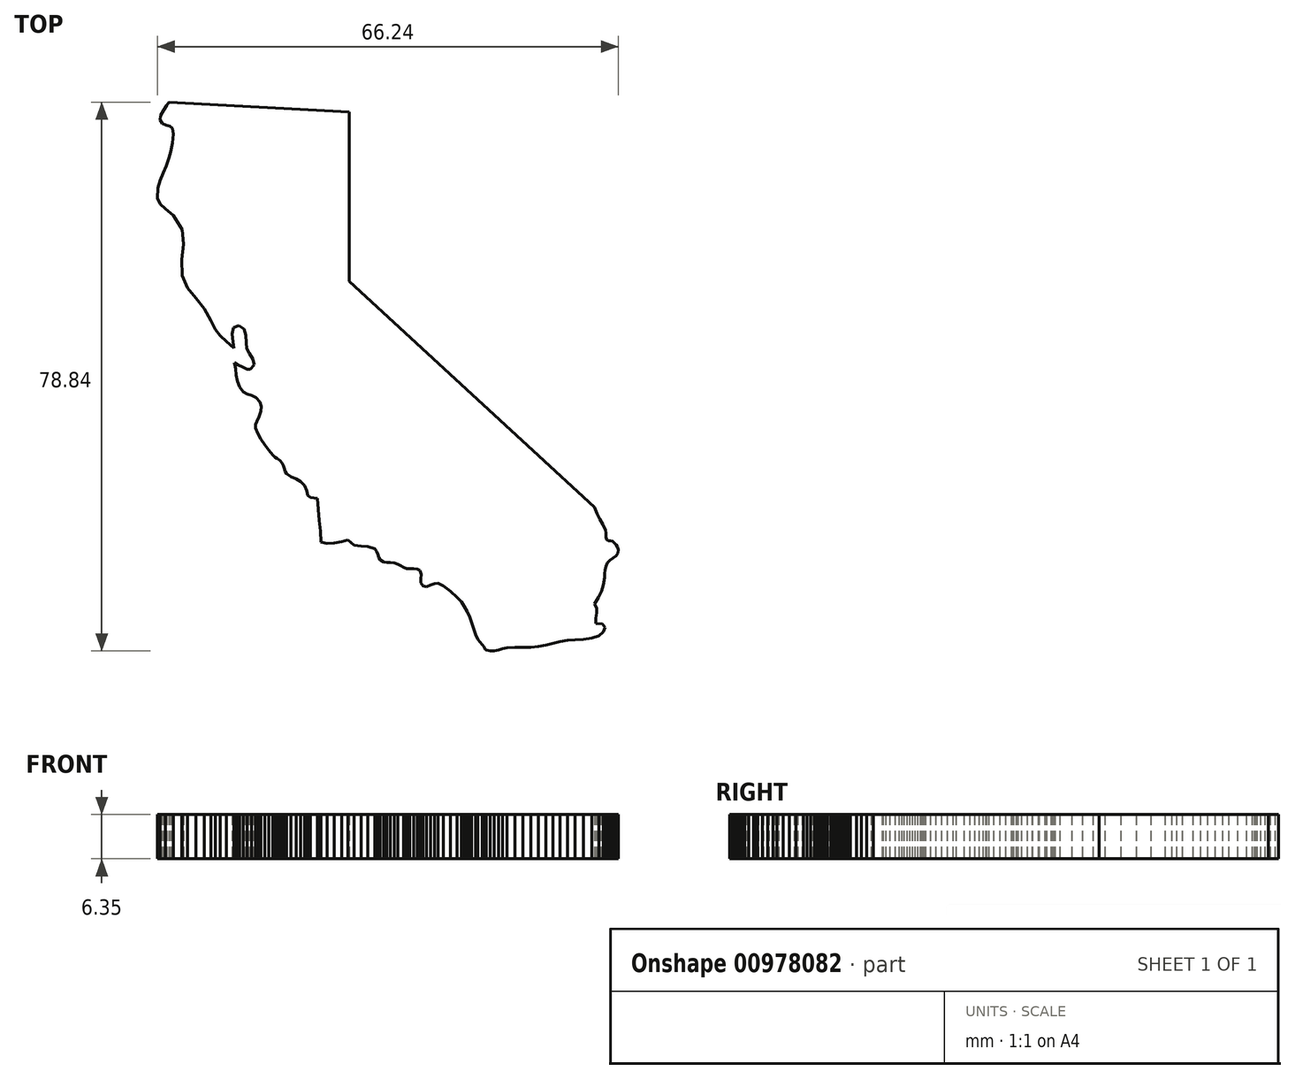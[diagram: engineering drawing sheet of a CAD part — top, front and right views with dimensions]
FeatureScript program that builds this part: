
annotation { "Feature Type Name" : "Feature", "Feature Type Description" : "" }
export const myFeature = defineFeature(function(context is Context, id is Id, definition is map)
    precondition{}
    {
        {
            var Q0;
            Q0=qCreatedBy(makeId("Top.planeOp"),FACE);
            var sketch = newSketch(context, id + "F0", { "sketchPlane" : qUnion([Q0])});
            skLineSegment(sketch, "E0", {"start": v(29.7, -18.77) * mm, "end": v(20.88, -10.66) * mm});
            skLineSegment(sketch, "E1", {"start": v(20.88, -10.66) * mm, "end": v(12.07, -2.55) * mm});
            skLineSegment(sketch, "E2", {"start": v(12.07, -2.55) * mm, "end": v(3.26, 5.56) * mm});
            skLineSegment(sketch, "E3", {"start": v(3.26, 5.56) * mm, "end": v(-5.55, 13.67) * mm});
            skLineSegment(sketch, "E4", {"start": v(-5.55, 13.67) * mm, "end": v(-5.55, 19.75) * mm});
            skLineSegment(sketch, "E5", {"start": v(-5.55, 19.75) * mm, "end": v(-5.55, 25.84) * mm});
            skLineSegment(sketch, "E6", {"start": v(-5.55, 25.84) * mm, "end": v(-5.55, 31.92) * mm});
            skLineSegment(sketch, "E7", {"start": v(-5.55, 31.92) * mm, "end": v(-5.55, 38) * mm});
            skLineSegment(sketch, "E8", {"start": v(-5.55, 38) * mm, "end": v(-12.02, 38.36) * mm});
            skLineSegment(sketch, "E9", {"start": v(-12.02, 38.36) * mm, "end": v(-18.5, 38.71) * mm});
            skLineSegment(sketch, "E10", {"start": v(-18.5, 38.71) * mm, "end": v(-24.97, 39.07) * mm});
            skLineSegment(sketch, "E11", {"start": v(-24.97, 39.07) * mm, "end": v(-31.45, 39.42) * mm});
            skLineSegment(sketch, "E12", {"start": v(-31.45, 39.42) * mm, "end": v(-31.76, 38.93) * mm});
            skLineSegment(sketch, "E13", {"start": v(-31.76, 38.93) * mm, "end": v(-32.24, 38.24) * mm});
            skLineSegment(sketch, "E14", {"start": v(-32.24, 38.24) * mm, "end": v(-32.64, 37.5) * mm});
            skLineSegment(sketch, "E15", {"start": v(-32.64, 37.5) * mm, "end": v(-32.73, 36.84) * mm});
            skLineSegment(sketch, "E16", {"start": v(-32.73, 36.84) * mm, "end": v(-32.4, 36.36) * mm});
            skLineSegment(sketch, "E17", {"start": v(-32.4, 36.36) * mm, "end": v(-31.87, 36.12) * mm});
            skLineSegment(sketch, "E18", {"start": v(-31.87, 36.12) * mm, "end": v(-31.32, 35.95) * mm});
            skLineSegment(sketch, "E19", {"start": v(-31.32, 35.95) * mm, "end": v(-30.93, 35.65) * mm});
            skLineSegment(sketch, "E20", {"start": v(-30.93, 35.65) * mm, "end": v(-30.8, 34.8) * mm});
            skLineSegment(sketch, "E21", {"start": v(-30.8, 34.8) * mm, "end": v(-30.95, 33.55) * mm});
            skLineSegment(sketch, "E22", {"start": v(-30.95, 33.55) * mm, "end": v(-31.2, 32.28) * mm});
            skLineSegment(sketch, "E23", {"start": v(-31.2, 32.28) * mm, "end": v(-31.43, 31.37) * mm});
            skLineSegment(sketch, "E24", {"start": v(-31.43, 31.37) * mm, "end": v(-31.81, 30.28) * mm});
            skLineSegment(sketch, "E25", {"start": v(-31.81, 30.28) * mm, "end": v(-32.28, 29.24) * mm});
            skLineSegment(sketch, "E26", {"start": v(-32.28, 29.24) * mm, "end": v(-32.72, 28.2) * mm});
            skLineSegment(sketch, "E27", {"start": v(-32.72, 28.2) * mm, "end": v(-33.03, 27.1) * mm});
            skLineSegment(sketch, "E28", {"start": v(-33.03, 27.1) * mm, "end": v(-33.12, 25.63) * mm});
            skLineSegment(sketch, "E29", {"start": v(-33.12, 25.63) * mm, "end": v(-32.75, 24.77) * mm});
            skLineSegment(sketch, "E30", {"start": v(-32.75, 24.77) * mm, "end": v(-31.98, 24.08) * mm});
            skLineSegment(sketch, "E31", {"start": v(-31.98, 24.08) * mm, "end": v(-30.85, 23.15) * mm});
            skLineSegment(sketch, "E32", {"start": v(-30.85, 23.15) * mm, "end": v(-29.53, 21.1) * mm});
            skLineSegment(sketch, "E33", {"start": v(-29.53, 21.1) * mm, "end": v(-29.39, 19) * mm});
            skLineSegment(sketch, "E34", {"start": v(-29.39, 19) * mm, "end": v(-29.65, 16.8) * mm});
            skLineSegment(sketch, "E35", {"start": v(-29.65, 16.8) * mm, "end": v(-29.55, 14.5) * mm});
            skLineSegment(sketch, "E36", {"start": v(-29.55, 14.5) * mm, "end": v(-28.78, 12.76) * mm});
            skLineSegment(sketch, "E37", {"start": v(-28.78, 12.76) * mm, "end": v(-27.61, 11.26) * mm});
            skLineSegment(sketch, "E38", {"start": v(-27.61, 11.26) * mm, "end": v(-26.38, 9.75) * mm});
            skLineSegment(sketch, "E39", {"start": v(-26.38, 9.75) * mm, "end": v(-25.42, 8.01) * mm});
            skLineSegment(sketch, "E40", {"start": v(-25.42, 8.01) * mm, "end": v(-24.81, 6.77) * mm});
            skLineSegment(sketch, "E41", {"start": v(-24.81, 6.77) * mm, "end": v(-24.08, 5.84) * mm});
            skLineSegment(sketch, "E42", {"start": v(-24.08, 5.84) * mm, "end": v(-23.19, 5.02) * mm});
            skLineSegment(sketch, "E43", {"start": v(-23.19, 5.02) * mm, "end": v(-22.11, 4.07) * mm});
            skLineSegment(sketch, "E44", {"start": v(-22.11, 4.07) * mm, "end": v(-22.24, 4.98) * mm});
            skLineSegment(sketch, "E45", {"start": v(-22.24, 4.98) * mm, "end": v(-22.36, 6.11) * mm});
            skLineSegment(sketch, "E46", {"start": v(-22.36, 6.11) * mm, "end": v(-22.2, 7.03) * mm});
            skLineSegment(sketch, "E47", {"start": v(-22.2, 7.03) * mm, "end": v(-21.46, 7.32) * mm});
            skLineSegment(sketch, "E48", {"start": v(-21.46, 7.32) * mm, "end": v(-20.7, 6.84) * mm});
            skLineSegment(sketch, "E49", {"start": v(-20.7, 6.84) * mm, "end": v(-20.42, 5.93) * mm});
            skLineSegment(sketch, "E50", {"start": v(-20.42, 5.93) * mm, "end": v(-20.37, 4.89) * mm});
            skLineSegment(sketch, "E51", {"start": v(-20.37, 4.89) * mm, "end": v(-20.27, 4.02) * mm});
            skLineSegment(sketch, "E52", {"start": v(-20.27, 4.02) * mm, "end": v(-19.9, 3.34) * mm});
            skLineSegment(sketch, "E53", {"start": v(-19.9, 3.34) * mm, "end": v(-19.4, 2.52) * mm});
            skLineSegment(sketch, "E54", {"start": v(-19.4, 2.52) * mm, "end": v(-19.21, 1.7) * mm});
            skLineSegment(sketch, "E55", {"start": v(-19.21, 1.7) * mm, "end": v(-19.75, 1.06) * mm});
            skLineSegment(sketch, "E56", {"start": v(-19.75, 1.06) * mm, "end": v(-20.23, 1.07) * mm});
            skLineSegment(sketch, "E57", {"start": v(-20.23, 1.07) * mm, "end": v(-20.88, 1.34) * mm});
            skLineSegment(sketch, "E58", {"start": v(-20.88, 1.34) * mm, "end": v(-21.54, 1.7) * mm});
            skLineSegment(sketch, "E59", {"start": v(-21.54, 1.7) * mm, "end": v(-22.06, 1.99) * mm});
            skLineSegment(sketch, "E60", {"start": v(-22.06, 1.99) * mm, "end": v(-21.87, 1.1) * mm});
            skLineSegment(sketch, "E61", {"start": v(-21.87, 1.1) * mm, "end": v(-21.78, 0.22) * mm});
            skLineSegment(sketch, "E62", {"start": v(-21.78, 0.22) * mm, "end": v(-21.65, -0.65) * mm});
            skLineSegment(sketch, "E63", {"start": v(-21.65, -0.65) * mm, "end": v(-21.33, -1.5) * mm});
            skLineSegment(sketch, "E64", {"start": v(-21.33, -1.5) * mm, "end": v(-20.8, -2.2) * mm});
            skLineSegment(sketch, "E65", {"start": v(-20.8, -2.2) * mm, "end": v(-20.22, -2.5) * mm});
            skLineSegment(sketch, "E66", {"start": v(-20.22, -2.5) * mm, "end": v(-19.6, -2.68) * mm});
            skLineSegment(sketch, "E67", {"start": v(-19.6, -2.68) * mm, "end": v(-18.93, -3.04) * mm});
            skLineSegment(sketch, "E68", {"start": v(-18.93, -3.04) * mm, "end": v(-18.39, -3.62) * mm});
            skLineSegment(sketch, "E69", {"start": v(-18.39, -3.62) * mm, "end": v(-18.18, -4.26) * mm});
            skLineSegment(sketch, "E70", {"start": v(-18.18, -4.26) * mm, "end": v(-18.24, -4.97) * mm});
            skLineSegment(sketch, "E71", {"start": v(-18.24, -4.97) * mm, "end": v(-18.5, -5.77) * mm});
            skLineSegment(sketch, "E72", {"start": v(-18.5, -5.77) * mm, "end": v(-18.81, -6.44) * mm});
            skLineSegment(sketch, "E73", {"start": v(-18.81, -6.44) * mm, "end": v(-19.03, -6.88) * mm});
            skLineSegment(sketch, "E74", {"start": v(-19.03, -6.88) * mm, "end": v(-19.02, -7.37) * mm});
            skLineSegment(sketch, "E75", {"start": v(-19.02, -7.37) * mm, "end": v(-18.7, -8.18) * mm});
            skLineSegment(sketch, "E76", {"start": v(-18.7, -8.18) * mm, "end": v(-18.25, -8.98) * mm});
            skLineSegment(sketch, "E77", {"start": v(-18.25, -8.98) * mm, "end": v(-17.71, -9.82) * mm});
            skLineSegment(sketch, "E78", {"start": v(-17.71, -9.82) * mm, "end": v(-17.13, -10.6) * mm});
            skLineSegment(sketch, "E79", {"start": v(-17.13, -10.6) * mm, "end": v(-16.55, -11.27) * mm});
            skLineSegment(sketch, "E80", {"start": v(-16.55, -11.27) * mm, "end": v(-16.22, -11.56) * mm});
            skLineSegment(sketch, "E81", {"start": v(-16.22, -11.56) * mm, "end": v(-15.88, -11.8) * mm});
            skLineSegment(sketch, "E82", {"start": v(-15.88, -11.8) * mm, "end": v(-15.54, -12.05) * mm});
            skLineSegment(sketch, "E83", {"start": v(-15.54, -12.05) * mm, "end": v(-15.2, -12.4) * mm});
            skLineSegment(sketch, "E84", {"start": v(-15.2, -12.4) * mm, "end": v(-15, -12.79) * mm});
            skLineSegment(sketch, "E85", {"start": v(-15, -12.79) * mm, "end": v(-14.9, -13.2) * mm});
            skLineSegment(sketch, "E86", {"start": v(-14.9, -13.2) * mm, "end": v(-14.78, -13.6) * mm});
            skLineSegment(sketch, "E87", {"start": v(-14.78, -13.6) * mm, "end": v(-14.55, -13.95) * mm});
            skLineSegment(sketch, "E88", {"start": v(-14.55, -13.95) * mm, "end": v(-13.91, -14.4) * mm});
            skLineSegment(sketch, "E89", {"start": v(-13.91, -14.4) * mm, "end": v(-13.2, -14.73) * mm});
            skLineSegment(sketch, "E90", {"start": v(-13.2, -14.73) * mm, "end": v(-12.51, -15.1) * mm});
            skLineSegment(sketch, "E91", {"start": v(-12.51, -15.1) * mm, "end": v(-11.97, -15.68) * mm});
            skLineSegment(sketch, "E92", {"start": v(-11.97, -15.68) * mm, "end": v(-11.67, -16.43) * mm});
            skLineSegment(sketch, "E93", {"start": v(-11.67, -16.43) * mm, "end": v(-11.53, -17.03) * mm});
            skLineSegment(sketch, "E94", {"start": v(-11.53, -17.03) * mm, "end": v(-11.14, -17.4) * mm});
            skLineSegment(sketch, "E95", {"start": v(-11.14, -17.4) * mm, "end": v(-10.14, -17.49) * mm});
            skLineSegment(sketch, "E96", {"start": v(-10.14, -17.49) * mm, "end": v(-10.01, -19.08) * mm});
            skLineSegment(sketch, "E97", {"start": v(-10.01, -19.08) * mm, "end": v(-9.85, -20.64) * mm});
            skLineSegment(sketch, "E98", {"start": v(-9.85, -20.64) * mm, "end": v(-9.7, -22.2) * mm});
            skLineSegment(sketch, "E99", {"start": v(-9.7, -22.2) * mm, "end": v(-9.65, -23.8) * mm});
            skLineSegment(sketch, "E100", {"start": v(-9.65, -23.8) * mm, "end": v(-8.74, -23.96) * mm});
            skLineSegment(sketch, "E101", {"start": v(-8.74, -23.96) * mm, "end": v(-7.7, -23.88) * mm});
            skLineSegment(sketch, "E102", {"start": v(-7.7, -23.88) * mm, "end": v(-6.66, -23.69) * mm});
            skLineSegment(sketch, "E103", {"start": v(-6.66, -23.69) * mm, "end": v(-5.73, -23.49) * mm});
            skLineSegment(sketch, "E104", {"start": v(-5.73, -23.49) * mm, "end": v(-4.84, -24.2) * mm});
            skLineSegment(sketch, "E105", {"start": v(-4.84, -24.2) * mm, "end": v(-3.87, -24.38) * mm});
            skLineSegment(sketch, "E106", {"start": v(-3.87, -24.38) * mm, "end": v(-2.88, -24.43) * mm});
            skLineSegment(sketch, "E107", {"start": v(-2.88, -24.43) * mm, "end": v(-1.9, -24.76) * mm});
            skLineSegment(sketch, "E108", {"start": v(-1.9, -24.76) * mm, "end": v(-1.59, -25.11) * mm});
            skLineSegment(sketch, "E109", {"start": v(-1.59, -25.11) * mm, "end": v(-1.42, -25.56) * mm});
            skLineSegment(sketch, "E110", {"start": v(-1.42, -25.56) * mm, "end": v(-1.3, -26) * mm});
            skLineSegment(sketch, "E111", {"start": v(-1.3, -26) * mm, "end": v(-1.12, -26.32) * mm});
            skLineSegment(sketch, "E112", {"start": v(-1.12, -26.32) * mm, "end": v(-0.62, -26.63) * mm});
            skLineSegment(sketch, "E113", {"start": v(-0.62, -26.63) * mm, "end": v(-0.15, -26.7) * mm});
            skLineSegment(sketch, "E114", {"start": v(-0.15, -26.7) * mm, "end": v(0.36, -26.7) * mm});
            skLineSegment(sketch, "E115", {"start": v(0.36, -26.7) * mm, "end": v(0.95, -26.78) * mm});
            skLineSegment(sketch, "E116", {"start": v(0.95, -26.78) * mm, "end": v(1.4, -26.95) * mm});
            skLineSegment(sketch, "E117", {"start": v(1.4, -26.95) * mm, "end": v(1.82, -27.18) * mm});
            skLineSegment(sketch, "E118", {"start": v(1.82, -27.18) * mm, "end": v(2.24, -27.4) * mm});
            skLineSegment(sketch, "E119", {"start": v(2.24, -27.4) * mm, "end": v(2.68, -27.58) * mm});
            skLineSegment(sketch, "E120", {"start": v(2.68, -27.58) * mm, "end": v(3.17, -27.62) * mm});
            skLineSegment(sketch, "E121", {"start": v(3.17, -27.62) * mm, "end": v(3.71, -27.6) * mm});
            skLineSegment(sketch, "E122", {"start": v(3.71, -27.6) * mm, "end": v(4.22, -27.63) * mm});
            skLineSegment(sketch, "E123", {"start": v(4.22, -27.63) * mm, "end": v(4.63, -27.87) * mm});
            skLineSegment(sketch, "E124", {"start": v(4.63, -27.87) * mm, "end": v(4.8, -28.4) * mm});
            skLineSegment(sketch, "E125", {"start": v(4.8, -28.4) * mm, "end": v(4.74, -29.02) * mm});
            skLineSegment(sketch, "E126", {"start": v(4.74, -29.02) * mm, "end": v(4.73, -29.61) * mm});
            skLineSegment(sketch, "E127", {"start": v(4.73, -29.61) * mm, "end": v(5.05, -30.08) * mm});
            skLineSegment(sketch, "E128", {"start": v(5.05, -30.08) * mm, "end": v(5.57, -30.17) * mm});
            skLineSegment(sketch, "E129", {"start": v(5.57, -30.17) * mm, "end": v(6.15, -29.97) * mm});
            skLineSegment(sketch, "E130", {"start": v(6.15, -29.97) * mm, "end": v(6.72, -29.72) * mm});
            skLineSegment(sketch, "E131", {"start": v(6.72, -29.72) * mm, "end": v(7.23, -29.66) * mm});
            skLineSegment(sketch, "E132", {"start": v(7.23, -29.66) * mm, "end": v(7.98, -30.06) * mm});
            skLineSegment(sketch, "E133", {"start": v(7.98, -30.06) * mm, "end": v(8.97, -30.83) * mm});
            skLineSegment(sketch, "E134", {"start": v(8.97, -30.83) * mm, "end": v(9.92, -31.69) * mm});
            skLineSegment(sketch, "E135", {"start": v(9.92, -31.69) * mm, "end": v(10.55, -32.35) * mm});
            skLineSegment(sketch, "E136", {"start": v(10.55, -32.35) * mm, "end": v(10.98, -32.98) * mm});
            skLineSegment(sketch, "E137", {"start": v(10.98, -32.98) * mm, "end": v(11.4, -33.76) * mm});
            skLineSegment(sketch, "E138", {"start": v(11.4, -33.76) * mm, "end": v(11.75, -34.56) * mm});
            skLineSegment(sketch, "E139", {"start": v(11.75, -34.56) * mm, "end": v(12.05, -35.32) * mm});
            skLineSegment(sketch, "E140", {"start": v(12.05, -35.32) * mm, "end": v(12.35, -36.27) * mm});
            skLineSegment(sketch, "E141", {"start": v(12.35, -36.27) * mm, "end": v(12.6, -37.06) * mm});
            skLineSegment(sketch, "E142", {"start": v(12.6, -37.06) * mm, "end": v(12.94, -37.77) * mm});
            skLineSegment(sketch, "E143", {"start": v(12.94, -37.77) * mm, "end": v(13.55, -38.5) * mm});
            skLineSegment(sketch, "E144", {"start": v(13.55, -38.5) * mm, "end": v(13.86, -38.9) * mm});
            skLineSegment(sketch, "E145", {"start": v(13.86, -38.9) * mm, "end": v(13.96, -39.14) * mm});
            skLineSegment(sketch, "E146", {"start": v(13.96, -39.14) * mm, "end": v(14.14, -39.3) * mm});
            skLineSegment(sketch, "E147", {"start": v(14.14, -39.3) * mm, "end": v(14.69, -39.42) * mm});
            skLineSegment(sketch, "E148", {"start": v(14.69, -39.42) * mm, "end": v(15.27, -39.42) * mm});
            skLineSegment(sketch, "E149", {"start": v(15.27, -39.42) * mm, "end": v(15.9, -39.27) * mm});
            skLineSegment(sketch, "E150", {"start": v(15.9, -39.27) * mm, "end": v(16.51, -39.08) * mm});
            skLineSegment(sketch, "E151", {"start": v(16.51, -39.08) * mm, "end": v(17.1, -38.95) * mm});
            skLineSegment(sketch, "E152", {"start": v(17.1, -38.95) * mm, "end": v(18.24, -38.9) * mm});
            skLineSegment(sketch, "E153", {"start": v(18.24, -38.9) * mm, "end": v(19.38, -38.91) * mm});
            skLineSegment(sketch, "E154", {"start": v(19.38, -38.91) * mm, "end": v(20.52, -38.91) * mm});
            skLineSegment(sketch, "E155", {"start": v(20.52, -38.91) * mm, "end": v(21.64, -38.79) * mm});
            skLineSegment(sketch, "E156", {"start": v(21.64, -38.79) * mm, "end": v(22.68, -38.56) * mm});
            skLineSegment(sketch, "E157", {"start": v(22.68, -38.56) * mm, "end": v(23.7, -38.31) * mm});
            skLineSegment(sketch, "E158", {"start": v(23.7, -38.31) * mm, "end": v(24.74, -38.07) * mm});
            skLineSegment(sketch, "E159", {"start": v(24.74, -38.07) * mm, "end": v(25.8, -37.88) * mm});
            skLineSegment(sketch, "E160", {"start": v(25.8, -37.88) * mm, "end": v(26.87, -37.8) * mm});
            skLineSegment(sketch, "E161", {"start": v(26.87, -37.8) * mm, "end": v(28.1, -37.72) * mm});
            skLineSegment(sketch, "E162", {"start": v(28.1, -37.72) * mm, "end": v(29.31, -37.57) * mm});
            skLineSegment(sketch, "E163", {"start": v(29.31, -37.57) * mm, "end": v(30.3, -37.25) * mm});
            skLineSegment(sketch, "E164", {"start": v(30.3, -37.25) * mm, "end": v(30.98, -36.67) * mm});
            skLineSegment(sketch, "E165", {"start": v(30.98, -36.67) * mm, "end": v(31.19, -36.01) * mm});
            skLineSegment(sketch, "E166", {"start": v(31.19, -36.01) * mm, "end": v(30.84, -35.53) * mm});
            skLineSegment(sketch, "E167", {"start": v(30.84, -35.53) * mm, "end": v(29.89, -35.45) * mm});
            skLineSegment(sketch, "E168", {"start": v(29.89, -35.45) * mm, "end": v(29.9, -34.72) * mm});
            skLineSegment(sketch, "E169", {"start": v(29.9, -34.72) * mm, "end": v(29.99, -33.94) * mm});
            skLineSegment(sketch, "E170", {"start": v(29.99, -33.94) * mm, "end": v(29.98, -33.22) * mm});
            skLineSegment(sketch, "E171", {"start": v(29.98, -33.22) * mm, "end": v(29.68, -32.64) * mm});
            skLineSegment(sketch, "E172", {"start": v(29.68, -32.64) * mm, "end": v(30.28, -31.72) * mm});
            skLineSegment(sketch, "E173", {"start": v(30.28, -31.72) * mm, "end": v(30.7, -30.85) * mm});
            skLineSegment(sketch, "E174", {"start": v(30.7, -30.85) * mm, "end": v(30.97, -29.92) * mm});
            skLineSegment(sketch, "E175", {"start": v(30.97, -29.92) * mm, "end": v(31.12, -28.84) * mm});
            skLineSegment(sketch, "E176", {"start": v(31.12, -28.84) * mm, "end": v(31.17, -28.31) * mm});
            skLineSegment(sketch, "E177", {"start": v(31.17, -28.31) * mm, "end": v(31.24, -27.78) * mm});
            skLineSegment(sketch, "E178", {"start": v(31.24, -27.78) * mm, "end": v(31.36, -27.26) * mm});
            skLineSegment(sketch, "E179", {"start": v(31.36, -27.26) * mm, "end": v(31.56, -26.79) * mm});
            skLineSegment(sketch, "E180", {"start": v(31.56, -26.79) * mm, "end": v(31.9, -26.4) * mm});
            skLineSegment(sketch, "E181", {"start": v(31.9, -26.4) * mm, "end": v(32.35, -26.05) * mm});
            skLineSegment(sketch, "E182", {"start": v(32.35, -26.05) * mm, "end": v(32.77, -25.72) * mm});
            skLineSegment(sketch, "E183", {"start": v(32.77, -25.72) * mm, "end": v(33.03, -25.37) * mm});
            skLineSegment(sketch, "E184", {"start": v(33.03, -25.37) * mm, "end": v(33.12, -24.86) * mm});
            skLineSegment(sketch, "E185", {"start": v(33.12, -24.86) * mm, "end": v(33, -24.47) * mm});
            skLineSegment(sketch, "E186", {"start": v(33, -24.47) * mm, "end": v(32.78, -24.14) * mm});
            skLineSegment(sketch, "E187", {"start": v(32.78, -24.14) * mm, "end": v(32.51, -23.83) * mm});
            skLineSegment(sketch, "E188", {"start": v(32.51, -23.83) * mm, "end": v(32.28, -23.68) * mm});
            skLineSegment(sketch, "E189", {"start": v(32.28, -23.68) * mm, "end": v(31.98, -23.62) * mm});
            skLineSegment(sketch, "E190", {"start": v(31.98, -23.62) * mm, "end": v(31.68, -23.56) * mm});
            skLineSegment(sketch, "E191", {"start": v(31.68, -23.56) * mm, "end": v(31.47, -23.44) * mm});
            skLineSegment(sketch, "E192", {"start": v(31.47, -23.44) * mm, "end": v(31.33, -23.1) * mm});
            skLineSegment(sketch, "E193", {"start": v(31.33, -23.1) * mm, "end": v(31.32, -22.76) * mm});
            skLineSegment(sketch, "E194", {"start": v(31.32, -22.76) * mm, "end": v(31.34, -22.42) * mm});
            skLineSegment(sketch, "E195", {"start": v(31.34, -22.42) * mm, "end": v(31.28, -22.08) * mm});
            skLineSegment(sketch, "E196", {"start": v(31.28, -22.08) * mm, "end": v(30.87, -21.21) * mm});
            skLineSegment(sketch, "E197", {"start": v(30.87, -21.21) * mm, "end": v(30.44, -20.49) * mm});
            skLineSegment(sketch, "E198", {"start": v(30.44, -20.49) * mm, "end": v(30.04, -19.73) * mm});
            skLineSegment(sketch, "E199", {"start": v(30.04, -19.73) * mm, "end": v(29.7, -18.77) * mm});
            skLineSegment(sketch, "E200", {"start": v(29.7, -18.77) * mm, "end": v(29.7, -18.95) * mm});
            skLineSegment(sketch, "E201", {"start": v(29.7, -18.95) * mm, "end": v(29.7, -19.14) * mm});
            skLineSegment(sketch, "E202", {"start": v(29.7, -19.14) * mm, "end": v(29.7, -19.33) * mm});
            skLineSegment(sketch, "E203", {"start": v(29.7, -19.33) * mm, "end": v(29.7, -19.51) * mm});
            skSolve(sketch);
        }
        {
            var Q0;
            Q0=makeQuery(id+"F0.imprint","IMPRINT",FACE,{"disambiguationData":[TD([[makeQuery(id+"F0.imprint","IMPRINT",EDGE,{"derivedFrom":sQuery(id+"F0.wireOp",EDGE,"E0")}),1.0]])]});
            extrude(context, id + "F1", {"entities" : qUnion([Q0]), "depth" : 6.35 * mm, "offsetDistance" : 25.4 * mm});
        }
    });
